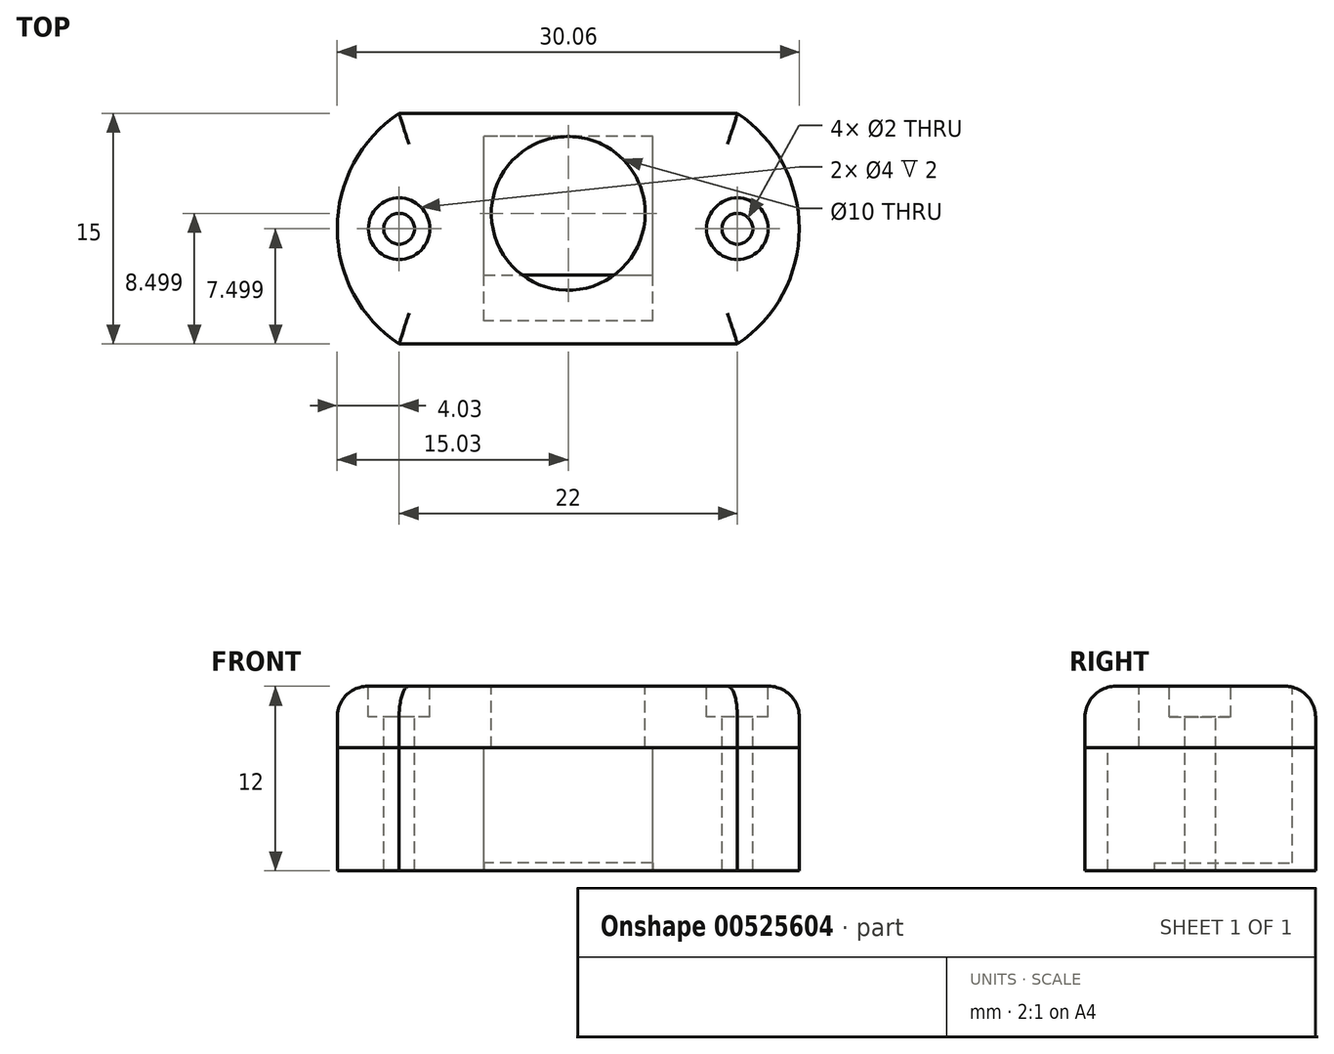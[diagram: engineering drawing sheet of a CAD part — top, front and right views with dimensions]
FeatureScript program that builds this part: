
annotation { "Feature Type Name" : "Feature", "Feature Type Description" : "" }
export const myFeature = defineFeature(function(context is Context, id is Id, definition is map)
    precondition{}
    {
        {
            var Q0;
            Q0=qCreatedBy(makeId("Top.planeOp"),FACE);
            var sketch = newSketch(context, id + "F0", { "sketchPlane" : qUnion([Q0])});
            skLineSegment(sketch, "E0.top", {"start": v(-34, -36.04) * mm, "end": v(-56, -36.04) * mm});
            skLineSegment(sketch, "E0.left", {"start": v(-34, -51.04) * mm, "end": v(-34, -36.04) * mm});
            skLineSegment(sketch, "E0.right", {"start": v(-56, -51.04) * mm, "end": v(-56, -36.04) * mm});
            skPoint(sketch, "E0.middle", {"position": v(-45, -43.54) * mm});
            skArc(sketch, "E1", {"start": v(-34, -51.04) * mm, "mid": v(-29.97, -43.54) * mm, "end": v(-34, -36.04) * mm});
            skArc(sketch, "E2", {"start": v(-56, -36.04) * mm, "mid": v(-60.03, -43.54) * mm, "end": v(-56, -51.04) * mm});
            skLineSegment(sketch, "E3", {"start": v(-56, -51.04) * mm, "end": v(-34, -51.04) * mm});
            skSolve(sketch);
        }
        {
            var Q0;
            Q0=qSketchRegion(id+"F0",true);
            extrude(context, id + "F1", {"entities" : qUnion([Q0]), "depth" : 8 * mm, "offsetDistance" : 25 * mm});
        }
        {
            var Q0;
            Q0=makeQuery(id+"F1.opExtrude","CAP_FACE",FACE,{"disambiguationData":[OSD([sQuery(id+"F0.wireOp",EDGE,"E0.bottom"),sQuery(id+"F0.wireOp",EDGE,"E0.top"),sQuery(id+"F0.wireOp",EDGE,"E0.left"),sQuery(id+"F0.wireOp",EDGE,"E0.right")])],"isStart":false});
            var sketch = newSketch(context, id + "F2", { "sketchPlane" : qUnion([Q0])});
            skCircle(sketch, "E4", {"center": v(-56, -43.54) * mm, "radius": 1 * mm});
            skCircle(sketch, "E5", {"center": v(-34, -43.54) * mm, "radius": 1 * mm});
            skCircle(sketch, "E6", {"center": v(-45, -43.54) * mm, "radius": 3.55 * mm, "construction": true});
            skLineSegment(sketch, "E7.bottom", {"start": v(-39.5, -49.54) * mm, "end": v(-50.5, -49.54) * mm});
            skLineSegment(sketch, "E7.top", {"start": v(-39.5, -37.54) * mm, "end": v(-50.5, -37.54) * mm});
            skLineSegment(sketch, "E7.left", {"start": v(-39.5, -49.54) * mm, "end": v(-39.5, -37.54) * mm});
            skLineSegment(sketch, "E7.right", {"start": v(-50.5, -49.54) * mm, "end": v(-50.5, -37.54) * mm});
            skSolve(sketch);
        }
        {
            var Q0;
            Q0=qSketchRegion(id+"F2",true);
            extrude(context, id + "F3", {"entities" : qUnion([Q0]), "operationType" : NewBodyOperationType.REMOVE, "oppositeDirection" : true, "depth" : 9 * mm, "offsetDistance" : 25 * mm});
        }
        {
            var Q0;
            Q0=makeQuery(id+"F1.opExtrude","CAP_FACE",FACE,{"disambiguationData":[OSD([sQuery(id+"F0.wireOp",EDGE,"E0.top"),sQuery(id+"F0.wireOp",EDGE,"E1"),sQuery(id+"F0.wireOp",EDGE,"E2"),sQuery(id+"F0.wireOp",EDGE,"E3")])],"isStart":true});
            var sketch = newSketch(context, id + "F4", { "sketchPlane" : qUnion([Q0])});
            skLineSegment(sketch, "E8.bottom", {"start": v(-50.5, 37.54) * mm, "end": v(-39.5, 37.54) * mm});
            skLineSegment(sketch, "E8.top", {"start": v(-50.5, 46.54) * mm, "end": v(-39.5, 46.54) * mm});
            skLineSegment(sketch, "E8.left", {"start": v(-50.5, 37.54) * mm, "end": v(-50.5, 46.54) * mm});
            skLineSegment(sketch, "E8.right", {"start": v(-39.5, 37.54) * mm, "end": v(-39.5, 46.54) * mm});
            skSolve(sketch);
        }
        {
            var Q0;
            Q0=qSketchRegion(id+"F4",true);
            extrude(context, id + "F5", {"entities" : qUnion([Q0]), "operationType" : NewBodyOperationType.ADD, "oppositeDirection" : true, "depth" : 0.5 * mm, "offsetDistance" : 25 * mm});
        }
        {
            var Q0;
            Q0=makeQuery(id+"F1.opExtrude","CAP_FACE",FACE,{"disambiguationData":[OSD([sQuery(id+"F0.wireOp",EDGE,"E0.top"),sQuery(id+"F0.wireOp",EDGE,"E1"),sQuery(id+"F0.wireOp",EDGE,"E2"),sQuery(id+"F0.wireOp",EDGE,"E3")])],"isStart":false});
            var sketch = newSketch(context, id + "F6", { "sketchPlane" : qUnion([Q0])});
            skLineSegment(sketch, "E9.top", {"start": v(-34, -36.04) * mm, "end": v(-56, -36.04) * mm});
            skLineSegment(sketch, "E9.left", {"start": v(-34, -51.04) * mm, "end": v(-34, -36.04) * mm});
            skLineSegment(sketch, "E9.right", {"start": v(-56, -51.04) * mm, "end": v(-56, -36.04) * mm});
            skPoint(sketch, "E9.middle", {"position": v(-45, -43.54) * mm});
            skArc(sketch, "E10", {"start": v(-34, -51.04) * mm, "mid": v(-29.97, -43.54) * mm, "end": v(-34, -36.04) * mm});
            skArc(sketch, "E11", {"start": v(-56, -36.04) * mm, "mid": v(-60.03, -43.54) * mm, "end": v(-56, -51.04) * mm});
            skLineSegment(sketch, "E12", {"start": v(-56, -51.04) * mm, "end": v(-34, -51.04) * mm});
            skPoint(sketch, "E13", {"position": v(-39.5, -43.54) * mm});
            skPoint(sketch, "E14", {"position": v(-45, -37.54) * mm});
            skSolve(sketch);
        }
        {
            var Q0;
            Q0=qSketchRegion(id+"F6",true);
            extrude(context, id + "F7", {"entities" : qUnion([Q0]), "depth" : 4 * mm, "offsetDistance" : 25 * mm});
        }
        {
            var Q0;
            Q0=makeQuery(id+"F7.opExtrude","CAP_FACE",FACE,{"disambiguationData":[OSD([sQuery(id+"F6.wireOp",EDGE,"E9.top"),sQuery(id+"F6.wireOp",EDGE,"E10"),sQuery(id+"F6.wireOp",EDGE,"E11"),sQuery(id+"F6.wireOp",EDGE,"E12")])],"isStart":false});
            var sketch = newSketch(context, id + "F8", { "sketchPlane" : qUnion([Q0])});
            skCircle(sketch, "E15", {"center": v(-56, -43.54) * mm, "radius": 1 * mm, "construction": true});
            skCircle(sketch, "E16", {"center": v(-34, -43.54) * mm, "radius": 1 * mm, "construction": true});
            skPoint(sketch, "E17", {"position": v(-29.97, -43.54) * mm});
            skPoint(sketch, "E18", {"position": v(-45, -51.04) * mm});
            skCircle(sketch, "E19", {"center": v(-45, -42.54) * mm, "radius": 5 * mm});
            skLineSegment(sketch, "E20.0", {"start": v(-39.5, -37.54) * mm, "end": v(-50.5, -37.54) * mm});
            skSolve(sketch);
        }
        {
            var Q0;
            Q0=qSketchRegion(id+"F8",true);
            extrude(context, id + "F9", {"entities" : qUnion([Q0]), "operationType" : NewBodyOperationType.REMOVE, "oppositeDirection" : true, "depth" : 4 * mm, "offsetDistance" : 25 * mm});
        }
        {
            var Q0;
            Q0=makeQuery(id+"F7.opExtrude","CAP_EDGE",EDGE,{"disambiguationData":[OSD([sQuery(id+"F6.wireOp",EDGE,"E10")])],"isStart":false});
            var Q1;
            Q1=makeQuery(id+"F7.opExtrude","CAP_EDGE",EDGE,{"disambiguationData":[OSD([sQuery(id+"F6.wireOp",EDGE,"E9.top")])],"isStart":false});
            var Q2;
            Q2=makeQuery(id+"F7.opExtrude","CAP_EDGE",EDGE,{"disambiguationData":[OSD([sQuery(id+"F6.wireOp",EDGE,"E11")])],"isStart":false});
            var Q3;
            Q3=makeQuery(id+"F7.opExtrude","CAP_EDGE",EDGE,{"disambiguationData":[OSD([sQuery(id+"F6.wireOp",EDGE,"E12")])],"isStart":false});
            fillet(context, id + "F10", {"entities" : qUnion([Q0, Q1, Q2, Q3]), "radius" : 2 * mm, "tangentPropagation" : true, "allowEdgeOverflow" : false});
        }
        {
            var Q0;
            Q0=sQuery(id+"F8.wireOp",VERTEX,"E16.center");
            var Q1;
            Q1=sQuery(id+"F8.wireOp",VERTEX,"E15.center");
            var Q2;
            Q2=makeQuery(id+"F7.opExtrude","SWEPT_BODY",BODY,{"disambiguationData":[OSD([sQuery(id+"F6.wireOp",EDGE,"E9.top"),sQuery(id+"F6.wireOp",EDGE,"E10"),sQuery(id+"F6.wireOp",EDGE,"E11"),sQuery(id+"F6.wireOp",EDGE,"E12")])]});
            hole(context, id + "F11", {"style" : HoleStyle.C_BORE, "endStyle" : HoleEndStyle.BLIND, "holeDiameter" : 2 * mm, "cBoreDiameter" : 4 * mm, "cBoreDepth" : 2 * mm, "majorDiameter" : 5 * mm, "holeDepth" : 20 * mm, "tappedDepth" : 12 * mm, "tapClearance" : 3, "locations" : qUnion([Q0, Q1]), "scope" : qUnion([Q2])});
        }
    });
